# Revit family: Haworth_Cappellini_Bac_Table_Round_EU_PRELIMINARY
name_source: partatom
category: Furniture
revit_build: Autodesk Revit 2018 (Build: 20170223_1515(x64)
units: mm (PartAtom-declared; Revit-internal decimal feet)

## family parameters
Always vertical = Yes
Cut with Voids When Loaded = No
OmniClass Number = 23.40.70.14.64.21
OmniClass Title = Systems Furniture
Room Calculation Point = No
Shared = No
Work Plane-Based = No

## types (1)
- Round Table
    Actual Depth = 125 cm
    Actual Height = 74 cm
    Actual Width = 125 cm
    Assembly Code = E2020200
    Description = Haworth - Cappellini - Bac - Table - Round
    Leg Depth = 10 cm
    Manufacturer = Haworth
    Model = BAC4
    Radius = 63 cm
    Revision Number = 4
    Size = Verify Final Dim. w/ Haworth
    Support Depth = 6 cm
    Support Height = 11 cm
    Table Thickness = 3 cm
    URL = https://www.haworth.com
    URL - Product = https://www.haworth.com
    Warranty = http://www.haworth.com

## geometry (parser evidence)
native form markers: Sweep x2
no freeform markers — native parametric forms only
